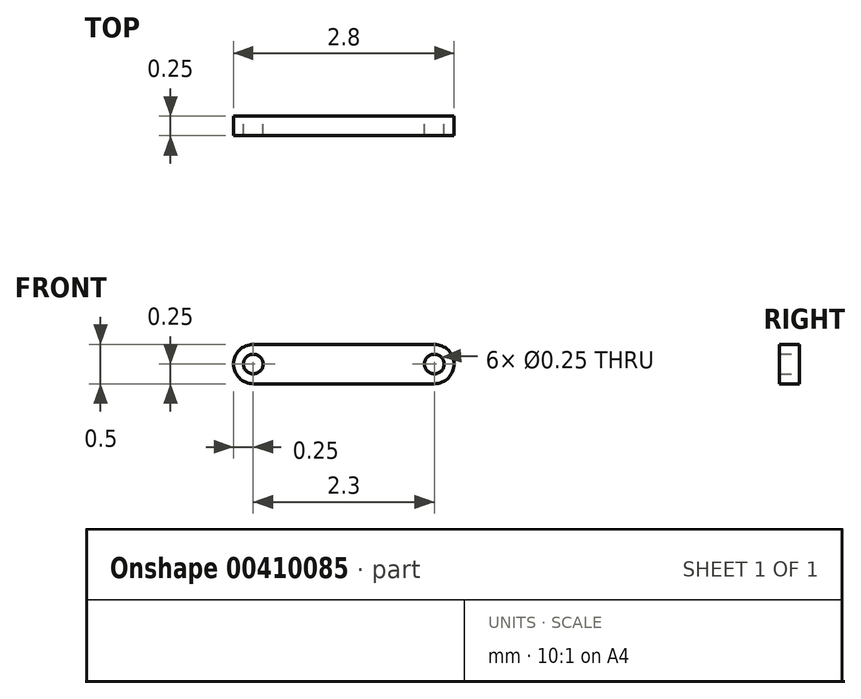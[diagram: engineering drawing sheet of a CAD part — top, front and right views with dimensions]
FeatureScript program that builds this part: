
annotation { "Feature Type Name" : "Feature", "Feature Type Description" : "" }
export const myFeature = defineFeature(function(context is Context, id is Id, definition is map)
    precondition{}
    {
        {
            var Q0;
            Q0=qCreatedBy(makeId("Front.planeOp"),FACE);
            var sketch = newSketch(context, id + "F0", { "sketchPlane" : qUnion([Q0])});
            skArc(sketch, "E0", {"start": v(0, 0.25) * mm, "mid": v(-0.25, 0) * mm, "end": v(0, -0.25) * mm});
            skArc(sketch, "E1", {"start": v(2.3, -0.25) * mm, "mid": v(2.55, 0) * mm, "end": v(2.3, 0.25) * mm});
            skLineSegment(sketch, "E2", {"start": v(0, 0.25) * mm, "end": v(2.3, 0.25) * mm});
            skLineSegment(sketch, "E3", {"start": v(0, -0.25) * mm, "end": v(2.3, -0.25) * mm});
            skCircle(sketch, "E4", {"center": v(0, 0) * mm, "radius": 0.12 * mm});
            skCircle(sketch, "E5", {"center": v(2.3, 0) * mm, "radius": 0.12 * mm});
            skSolve(sketch);
        }
        {
            var Q0;
            Q0=makeQuery(id+"F0.imprint","IMPRINT",FACE,{"disambiguationData":[TD([[makeQuery(id+"F0.imprint","IMPRINT",EDGE,{"derivedFrom":sQuery(id+"F0.wireOp",EDGE,"E0")}),1.0]])]});
            extrude(context, id + "F1", {"entities" : qUnion([Q0]), "depth" : 0.25 * mm});
        }
    });
